# Revit family: AV4050001_GRIF. DH SC PLCA ALUVIA
name_source: partatom
category: Plumbing Fixtures
units: mm (PartAtom-declared; Revit-internal decimal feet)

## family parameters
Always vertical = Yes
Cut with Voids When Loaded = No
Host = Wall
OmniClass Number = 23.31.11.17.15
OmniClass Title = Shower Disc Faucets
Part Type = Normal
Room Calculation Point = No
Round Connector Dimension = Use Diameter
Shared = No

## types (1)
- BALTA
    Alto = 861.68 mm
    Altura ducha = 2000 mm  [stored 6.56168 ft]
    Altura mezclador = 1200 mm
    Ancho = 310 mm
    Capacidad de flujo = 80 psi: 9,5 L/min
    Capacidad de flujo estimada real a 80 Psi = 9,5 L/min.
    Capacidad de flujo máximo a 80 psi = 7,3 L/min.
    Ciclo de vida de la unidad de cierre = 250.000 ciclos
    Creado por = IDD
    Description = Aluvia integra líneas y formas como las de una erosión aluvial, su forma robusta está
inspirada en el agua esculpiendo las rocas a través de los años dando paso a superficies
más suaves, amigables y limpias evitando que haya acumulación de impurezas. El conjunto
de manijas es el resultado de su diseño ergonómico, brindando un agarre cómodo sin
importar el agua y el jabón. La marcación indeleble sobre las manijas ofrecen la facilidad
de reconocer como regular la temperatura del agua.• Grifería ducha ultra ahorro consumo de 7,3 litros por minuto.
• Cierre fácil giro práctico de tan sólo 90º.
• Regadera con funciones de chorro, tipo lluvia o hidromasaje.
• Tecnología anti-taponamiento que impide el taponamiento y acumulación de impurezas.
• Cómodo brazo largo que permite bañarse a una mayor distancia de la pared.
• Fácil limpieza: Diseño que evita la acumulación de impurezas
    Fabricante = Corona
    Fecha de creación = 21/07/2020
    Garantía = 30 años
    Garantía Acabados = 5 años
    Manufacturer = Corona
    Material = Corona_Cromado
    Model = Grifería ducha sencilla palanca Aluvia
    Peso neto = 530 gr. - 1,16 lb
    Presión máxima recomendada = 125 psi (862 Kpa)
    Presión mínima recomendada = 20 psi (138 Kpa)
    Profundidad = 363 mm  [stored 1.19094 ft]
    Referencia = 414120001
    Temperatura de uso = 5ºC a 71ºC.
    Vida útil o desgaste (unidad) = 250.000 ciclos.

note: [stored X ft] marks values corroborated as IEEE doubles in the binary element streams (Revit-internal decimal feet)

## geometry (parser evidence)
native form markers: Sweep x14
no freeform markers — native parametric forms only
